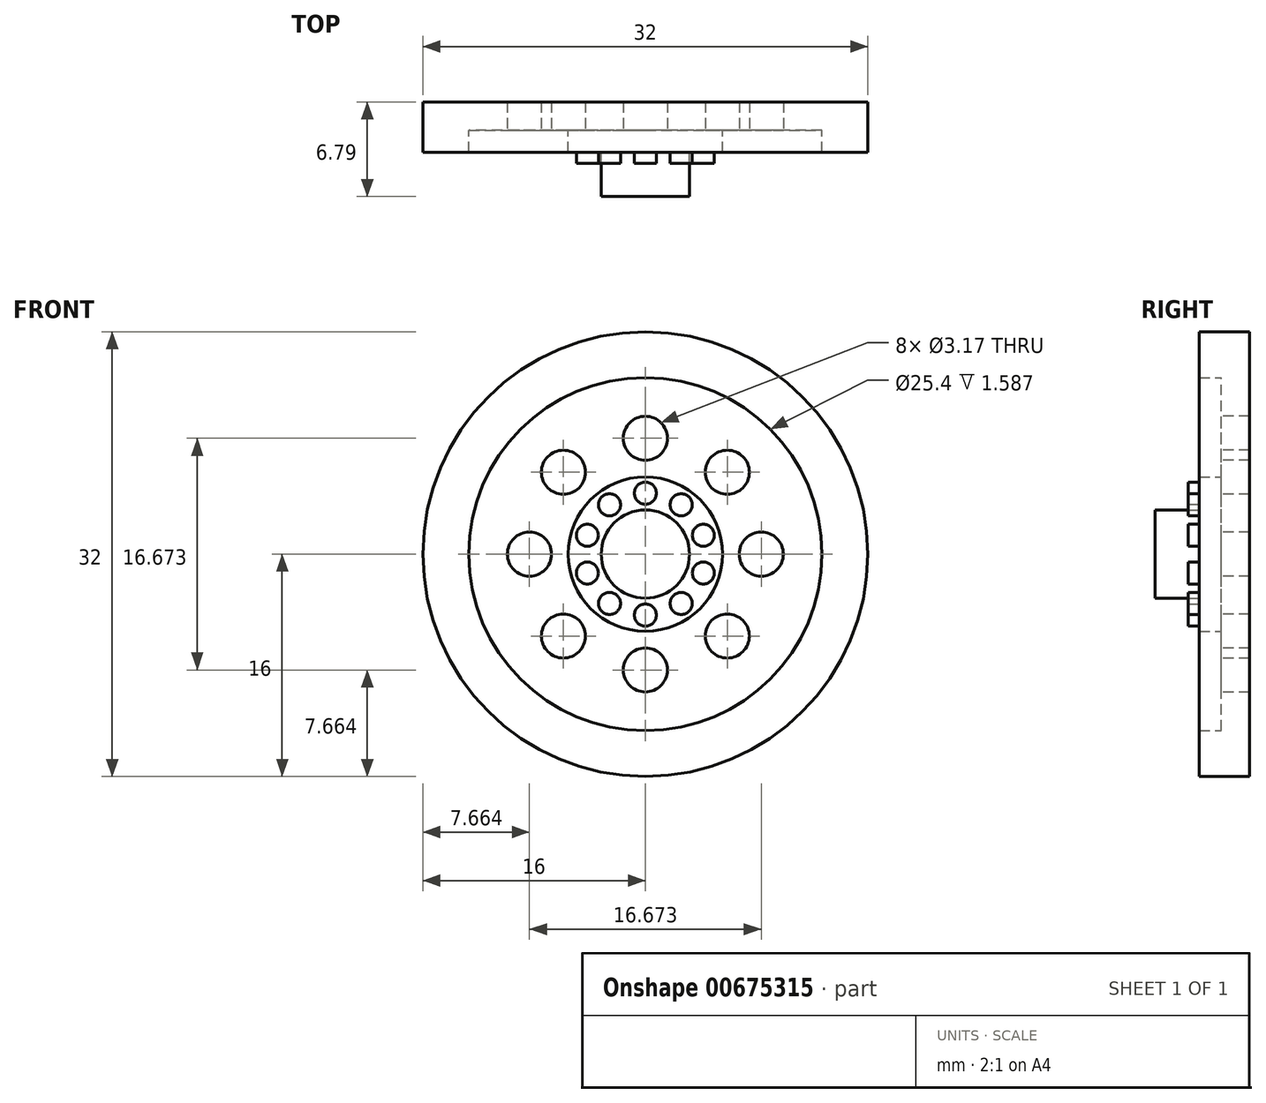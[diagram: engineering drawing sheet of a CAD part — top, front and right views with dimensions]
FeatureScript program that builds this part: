
annotation { "Feature Type Name" : "Feature", "Feature Type Description" : "" }
export const myFeature = defineFeature(function(context is Context, id is Id, definition is map)
    precondition{}
    {
        {
            var Q0;
            Q0=qCreatedBy(makeId("Front.planeOp"),FACE);
            var sketch = newSketch(context, id + "F0", { "sketchPlane" : qUnion([Q0])});
            skCircle(sketch, "E0", {"center": v(0, 0) * mm, "radius": 16 * mm});
            skSolve(sketch);
        }
        {
            var Q0;
            Q0=makeQuery(id+"F0.imprint","IMPRINT",FACE,{"disambiguationData":[TD([[makeQuery(id+"F0.imprint","IMPRINT",EDGE,{"derivedFrom":sQuery(id+"F0.wireOp",EDGE,"E0")}),1.0]])]});
            extrude(context, id + "F1", {"entities" : qUnion([Q0]), "depth" : 2.03 * mm, "offsetDistance" : 25.4 * mm});
        }
        {
            var Q0;
            Q0=makeQuery(id+"F1.opExtrude","CAP_FACE",FACE,{"disambiguationData":[OSD([sQuery(id+"F0.wireOp",EDGE,"E0")])],"isStart":false});
            var sketch = newSketch(context, id + "F2", { "sketchPlane" : qUnion([Q0])});
            skCircle(sketch, "E1", {"center": v(0, 8.34) * mm, "radius": 1.59 * mm});
            skCircle(sketch, "E2.1.0", {"center": v(-5.9, 5.9) * mm, "radius": 1.59 * mm});
            skCircle(sketch, "E2.2.0", {"center": v(-8.34, 0) * mm, "radius": 1.59 * mm});
            skCircle(sketch, "E2.3.0", {"center": v(-5.9, -5.9) * mm, "radius": 1.59 * mm});
            skCircle(sketch, "E2.4.0", {"center": v(0, -8.34) * mm, "radius": 1.59 * mm});
            skCircle(sketch, "E2.5.0", {"center": v(5.9, -5.9) * mm, "radius": 1.59 * mm});
            skCircle(sketch, "E2.6.0", {"center": v(8.34, 0) * mm, "radius": 1.59 * mm});
            skCircle(sketch, "E2.7.0", {"center": v(5.9, 5.9) * mm, "radius": 1.59 * mm});
            skPoint(sketch, "E2.center", {"position": v(0, 0) * mm});
            skSolve(sketch);
        }
        {
            var Q0;
            Q0=makeQuery(id+"F2.imprint","IMPRINT",FACE,{"disambiguationData":[TD([[makeQuery(id+"F2.imprint","IMPRINT",EDGE,{"derivedFrom":sQuery(id+"F2.wireOp",EDGE,"E1")}),1.0]])]});
            var Q1;
            Q1=makeQuery(id+"F2.imprint","IMPRINT",FACE,{"disambiguationData":[TD([[makeQuery(id+"F2.imprint","IMPRINT",EDGE,{"derivedFrom":sQuery(id+"F2.wireOp",EDGE,"E2.7.0")}),1.0]])]});
            var Q2;
            Q2=makeQuery(id+"F2.imprint","IMPRINT",FACE,{"disambiguationData":[TD([[makeQuery(id+"F2.imprint","IMPRINT",EDGE,{"derivedFrom":sQuery(id+"F2.wireOp",EDGE,"E2.6.0")}),1.0]])]});
            var Q3;
            Q3=makeQuery(id+"F2.imprint","IMPRINT",FACE,{"disambiguationData":[TD([[makeQuery(id+"F2.imprint","IMPRINT",EDGE,{"derivedFrom":sQuery(id+"F2.wireOp",EDGE,"E2.5.0")}),1.0]])]});
            var Q4;
            Q4=makeQuery(id+"F2.imprint","IMPRINT",FACE,{"disambiguationData":[TD([[makeQuery(id+"F2.imprint","IMPRINT",EDGE,{"derivedFrom":sQuery(id+"F2.wireOp",EDGE,"E2.3.0")}),1.0]])]});
            var Q5;
            Q5=makeQuery(id+"F2.imprint","IMPRINT",FACE,{"disambiguationData":[TD([[makeQuery(id+"F2.imprint","IMPRINT",EDGE,{"derivedFrom":sQuery(id+"F2.wireOp",EDGE,"E2.1.0")}),1.0]])]});
            var Q6;
            Q6=makeQuery(id+"F2.imprint","IMPRINT",FACE,{"disambiguationData":[TD([[makeQuery(id+"F2.imprint","IMPRINT",EDGE,{"derivedFrom":sQuery(id+"F2.wireOp",EDGE,"E2.2.0")}),1.0]])]});
            var Q7;
            Q7=makeQuery(id+"F2.imprint","IMPRINT",FACE,{"disambiguationData":[TD([[makeQuery(id+"F2.imprint","IMPRINT",EDGE,{"derivedFrom":sQuery(id+"F2.wireOp",EDGE,"E2.4.0")}),1.0]])]});
            extrude(context, id + "F3", {"entities" : qUnion([Q0, Q1, Q2, Q3, Q4, Q5, Q6, Q7]), "operationType" : NewBodyOperationType.REMOVE, "oppositeDirection" : true, "depth" : 20.32 * mm, "offsetDistance" : 25.4 * mm});
        }
        {
            var Q0;
            Q0=makeQuery(id+"F1.opExtrude","CAP_FACE",FACE,{"disambiguationData":[OSD([sQuery(id+"F0.wireOp",EDGE,"E0")])],"isStart":false});
            var sketch = newSketch(context, id + "F4", { "sketchPlane" : qUnion([Q0])});
            skCircle(sketch, "E3", {"center": v(0, 0) * mm, "radius": 5.56 * mm});
            skSolve(sketch);
        }
        {
            var Q0;
            Q0=makeQuery(id+"F4.imprint","IMPRINT",FACE,{"disambiguationData":[TD([[makeQuery(id+"F4.imprint","IMPRINT",EDGE,{"derivedFrom":sQuery(id+"F4.wireOp",EDGE,"E3")}),1.0]])]});
            extrude(context, id + "F5", {"entities" : qUnion([Q0]), "operationType" : NewBodyOperationType.ADD, "depth" : 1.59 * mm, "offsetDistance" : 25.4 * mm});
        }
        {
            var Q0;
            Q0=makeQuery(id+"F5.opExtrude","CAP_FACE",FACE,{"disambiguationData":[OSD([sQuery(id+"F4.wireOp",EDGE,"E3")])],"isStart":false});
            var sketch = newSketch(context, id + "F6", { "sketchPlane" : qUnion([Q0])});
            skCircle(sketch, "E4", {"center": v(0, 0) * mm, "radius": 3.18 * mm});
            skSolve(sketch);
        }
        {
            var Q0;
            Q0=makeQuery(id+"F6.imprint","IMPRINT",FACE,{"disambiguationData":[TD([[makeQuery(id+"F6.imprint","IMPRINT",EDGE,{"derivedFrom":sQuery(id+"F6.wireOp",EDGE,"E4")}),1.0]])]});
            extrude(context, id + "F7", {"entities" : qUnion([Q0]), "operationType" : NewBodyOperationType.ADD, "depth" : 3.17 * mm, "offsetDistance" : 25.4 * mm});
        }
        {
            var Q0;
            Q0=makeQuery(id+"F5.opExtrude","CAP_FACE",FACE,{"disambiguationData":[OSD([sQuery(id+"F4.wireOp",EDGE,"E3")])],"isStart":false});
            var sketch = newSketch(context, id + "F8", { "sketchPlane" : qUnion([Q0])});
            skCircle(sketch, "E5", {"center": v(0, 4.39) * mm, "radius": 0.8 * mm});
            skCircle(sketch, "E6.1.0", {"center": v(-2.58, 3.55) * mm, "radius": 0.8 * mm});
            skCircle(sketch, "E6.2.0", {"center": v(-4.17, 1.36) * mm, "radius": 0.8 * mm});
            skCircle(sketch, "E6.3.0", {"center": v(-4.17, -1.36) * mm, "radius": 0.8 * mm});
            skCircle(sketch, "E6.4.0", {"center": v(-2.58, -3.55) * mm, "radius": 0.8 * mm});
            skCircle(sketch, "E6.5.0", {"center": v(0, -4.39) * mm, "radius": 0.8 * mm});
            skCircle(sketch, "E6.6.0", {"center": v(2.58, -3.55) * mm, "radius": 0.8 * mm});
            skCircle(sketch, "E6.7.0", {"center": v(4.17, -1.36) * mm, "radius": 0.8 * mm});
            skCircle(sketch, "E6.8.0", {"center": v(4.17, 1.36) * mm, "radius": 0.8 * mm});
            skCircle(sketch, "E6.9.0", {"center": v(2.58, 3.55) * mm, "radius": 0.8 * mm});
            skPoint(sketch, "E6.center", {"position": v(0, 0) * mm});
            skSolve(sketch);
        }
        {
            var Q0;
            Q0=makeQuery(id+"F8.imprint","IMPRINT",FACE,{"disambiguationData":[TD([[makeQuery(id+"F8.imprint","IMPRINT",EDGE,{"derivedFrom":sQuery(id+"F8.wireOp",EDGE,"E5")}),1.0]])]});
            var Q1;
            Q1=makeQuery(id+"F8.imprint","IMPRINT",FACE,{"disambiguationData":[TD([[makeQuery(id+"F8.imprint","IMPRINT",EDGE,{"derivedFrom":sQuery(id+"F8.wireOp",EDGE,"E6.9.0")}),1.0]])]});
            var Q2;
            Q2=makeQuery(id+"F8.imprint","IMPRINT",FACE,{"disambiguationData":[TD([[makeQuery(id+"F8.imprint","IMPRINT",EDGE,{"derivedFrom":sQuery(id+"F8.wireOp",EDGE,"E6.8.0")}),1.0]])]});
            var Q3;
            Q3=makeQuery(id+"F8.imprint","IMPRINT",FACE,{"disambiguationData":[TD([[makeQuery(id+"F8.imprint","IMPRINT",EDGE,{"derivedFrom":sQuery(id+"F8.wireOp",EDGE,"E6.6.0")}),1.0]])]});
            var Q4;
            Q4=makeQuery(id+"F8.imprint","IMPRINT",FACE,{"disambiguationData":[TD([[makeQuery(id+"F8.imprint","IMPRINT",EDGE,{"derivedFrom":sQuery(id+"F8.wireOp",EDGE,"E6.7.0")}),1.0]])]});
            var Q5;
            Q5=makeQuery(id+"F8.imprint","IMPRINT",FACE,{"disambiguationData":[TD([[makeQuery(id+"F8.imprint","IMPRINT",EDGE,{"derivedFrom":sQuery(id+"F8.wireOp",EDGE,"E6.5.0")}),1.0]])]});
            var Q6;
            Q6=makeQuery(id+"F8.imprint","IMPRINT",FACE,{"disambiguationData":[TD([[makeQuery(id+"F8.imprint","IMPRINT",EDGE,{"derivedFrom":sQuery(id+"F8.wireOp",EDGE,"E6.4.0")}),1.0]])]});
            var Q7;
            Q7=makeQuery(id+"F8.imprint","IMPRINT",FACE,{"disambiguationData":[TD([[makeQuery(id+"F8.imprint","IMPRINT",EDGE,{"derivedFrom":sQuery(id+"F8.wireOp",EDGE,"E6.3.0")}),1.0]])]});
            var Q8;
            Q8=makeQuery(id+"F8.imprint","IMPRINT",FACE,{"disambiguationData":[TD([[makeQuery(id+"F8.imprint","IMPRINT",EDGE,{"derivedFrom":sQuery(id+"F8.wireOp",EDGE,"E6.2.0")}),1.0]])]});
            var Q9;
            Q9=makeQuery(id+"F8.imprint","IMPRINT",FACE,{"disambiguationData":[TD([[makeQuery(id+"F8.imprint","IMPRINT",EDGE,{"derivedFrom":sQuery(id+"F8.wireOp",EDGE,"E6.1.0")}),1.0]])]});
            extrude(context, id + "F9", {"entities" : qUnion([Q0, Q1, Q2, Q3, Q4, Q5, Q6, Q7, Q8, Q9]), "operationType" : NewBodyOperationType.ADD, "depth" : 0.8 * mm, "offsetDistance" : 25.4 * mm});
        }
        {
            var Q0;
            Q0=makeQuery(id+"F0.imprint","IMPRINT",FACE,{"disambiguationData":[TD([[makeQuery(id+"F0.imprint","IMPRINT",EDGE,{"derivedFrom":sQuery(id+"F0.wireOp",EDGE,"E0")}),1.0]])]});
            var sketch = newSketch(context, id + "F10", { "sketchPlane" : qUnion([Q0])});
            skCircle(sketch, "E7", {"center": v(0, 0) * mm, "radius": 3.17 * mm});
            skSolve(sketch);
        }
        {
            var Q0;
            Q0=sQuery(id+"F10.wireOp",EDGE,"E7");
            extrude(context, id + "F11", {"bodyType" : ToolBodyType.SURFACE, "surfaceEntities" : qUnion([Q0]), "oppositeDirection" : true, "depth" : 9.52 * mm, "offsetDistance" : 25.4 * mm});
        }
        {
            var Q0;
            Q0=makeQuery(id+"F1.opExtrude","CAP_FACE",FACE,{"disambiguationData":[OSD([sQuery(id+"F0.wireOp",EDGE,"E0")])],"isStart":false});
            var sketch = newSketch(context, id + "F12", { "sketchPlane" : qUnion([Q0])});
            skCircle(sketch, "E8", {"center": v(0, 0) * mm, "radius": 12.7 * mm});
            skSolve(sketch);
        }
        {
            var Q0;
            Q0=makeQuery(id+"F12.imprint","IMPRINT",FACE,{"disambiguationData":[TD([[makeQuery(id+"F12.imprint","IMPRINT",EDGE,{"derivedFrom":sQuery(id+"F12.wireOp",EDGE,"E8")}),-1.0]])]});
            extrude(context, id + "F13", {"entities" : qUnion([Q0]), "operationType" : NewBodyOperationType.ADD, "depth" : 1.59 * mm, "offsetDistance" : 25.4 * mm});
        }
    });
